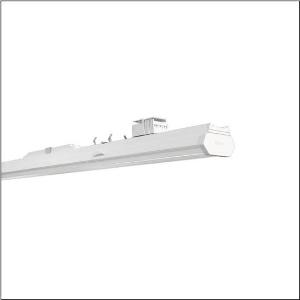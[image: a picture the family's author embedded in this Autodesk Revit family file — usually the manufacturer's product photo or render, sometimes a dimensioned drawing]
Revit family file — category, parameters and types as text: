
# Revit family: licross_r__21_protected_ho_52td1bmn4exm_7a17
name_source: partatom
category: Lighting Fixtures
units: mm (PartAtom-declared; Revit-internal decimal feet)

## family parameters
Cut with Voids When Loaded = No
Host = Face
Light Source = No
Part Type = Normal
Room Calculation Point = No
Round Connector Dimension = Use Diameter
Shared = No

## types (1)
- --- (1 x LED, 14040 lm, 83.2 W, 4000K)
    Apparent Load = 83 VA
    CIE Flux Codes = 54 82 95 97 100
    Color Rendering = 80
    Color Temperature = 4000K
    Default Elevation = 1800 mm
    Description = Licross® 21 Protected HO, luminaire insert, of sheet steel, galvanised, coil coated, white, length: 1.500mm, width: 90mm, height: 103mm, LED rated luminous flux: 14.040lm, light colour: 840, control gear: ON/OFF Multilumen, with plug, 3-pole, with phase selection, mains connection: 220..240V, AC, 50/60Hz, rated input power: 83W, halogen-free wiring, primary optical cover: cover, of PMMA, light emission: direct distribution, primary light characteristic: symmetric, protection rating (complete): IP54, insulation class (complete): insulation class I (protective earthing), certification: CE, ENEC, VDE, UKCA, protection symbol: D if used in an environment with non-conductive dust loads with corresponding accessories, impact resistance: IK06, permissible ambient temperature for indoor applications: -35..+35°C, corresponds to IFS (International Featured Standards) requirements for safety and quality in the food industry, reducing of maximum allowable ambient temperature of 5°C with ceiling mounting, LABS conformity tested according to VDMA 24364:2018-05, packaging unit: 1 piece
    Height = 92 mm
    Lamp = 1 x LED
    Lamp Light Flux = 14040 lm
    Lamp Power = 83.2 W
    Lamp count = 1
    Length = 1500 mm
    Luminous efficacy = 169 lm/W
    Manufacturer = Siteco
    ModVariant = No
    Model = 52TD1BMN4EXM
    Mounting Place = Ceiling
    Mounting Type = Pendant
    Number of Poles = 1
    OnlyDefault = Yes
    Power Factor = 1
    Product Name = Licross® 21 Protected HO
    Product group = luminaire insert
    ProductGroupID = 901
    Protection Class = Protection class I
    Protection Degree = IP 54
    RLX_Detail_Level = 1
    RLX_Emergency_Light_Flux = 0 lm
    RLX_Emergency_Type = 0
    RLX_Emergency_Type_DB = No
    RlxData = <blob elided: 22049 chars, md5=32ede51a>
    Socket = socket
    Standby Power = 0 W
    System Light Flux = 14040 lm
    System Power = 83 W
    Type Comments = factory setting: luminous flux: 100 % | (A | C | E) | 195 mA
    Type Image = l_1256148.jpg
    URL = http://relux.com
    VarID = @adj_057493
    Voltage = 0 V
    Weight = 0.00 kg
    Width = 88 mm

## geometry (parser evidence)
native form markers: Blend x4, Sweep x10
no freeform markers — native parametric forms only
